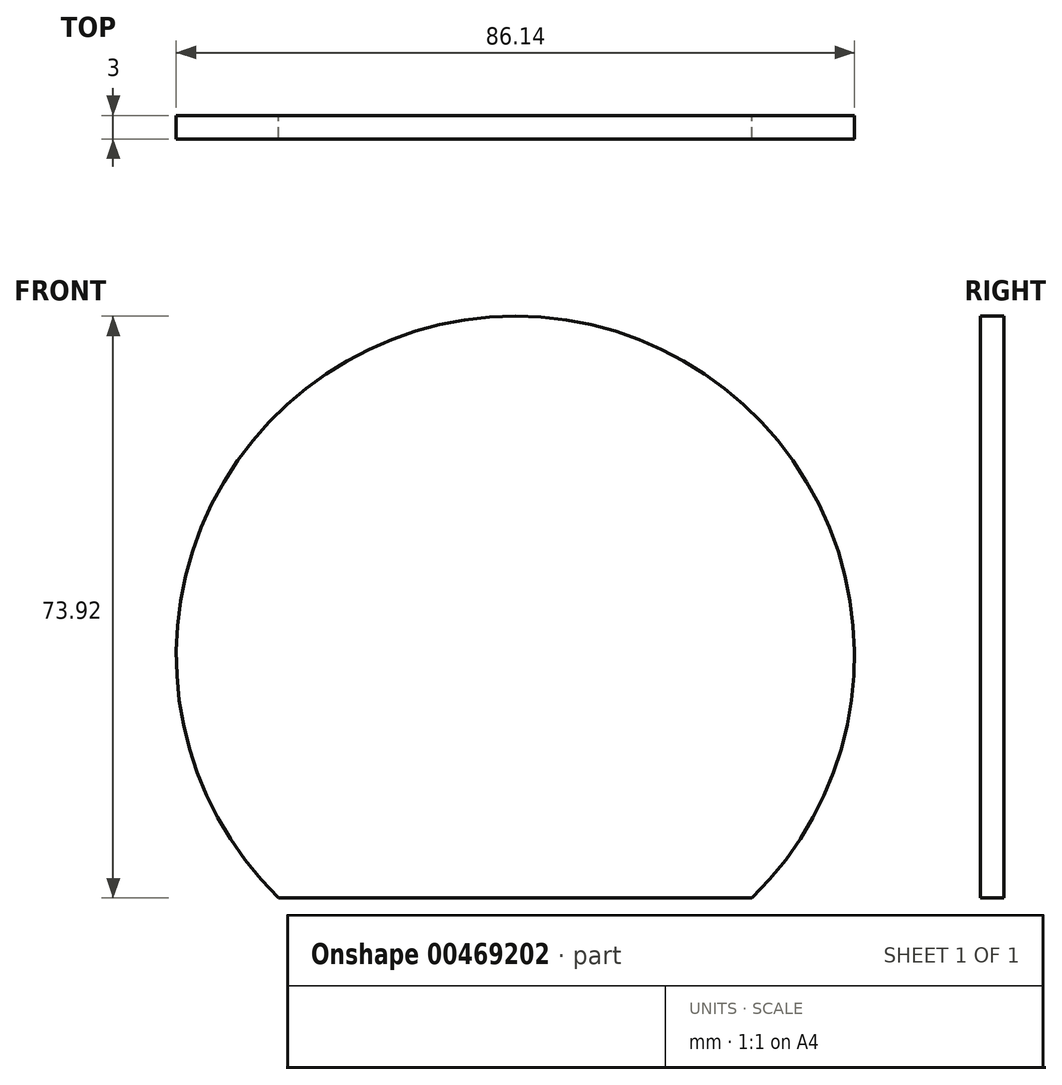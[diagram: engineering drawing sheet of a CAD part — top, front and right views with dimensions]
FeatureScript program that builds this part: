
annotation { "Feature Type Name" : "Feature", "Feature Type Description" : "" }
export const myFeature = defineFeature(function(context is Context, id is Id, definition is map)
    precondition{}
    {
        {
            var Q0;
            Q0=qCreatedBy(makeId("Front.planeOp"),FACE);
            var sketch = newSketch(context, id + "F0", { "sketchPlane" : qUnion([Q0])});
            skArc(sketch, "E0", {"start": v(30.05, -30.85) * mm, "mid": v(0, 43.07) * mm, "end": v(-30.05, -30.85) * mm});
            skLineSegment(sketch, "E1", {"start": v(-30.05, -30.85) * mm, "end": v(25.18, -30.85) * mm});
            skLineSegment(sketch, "E2", {"start": v(25.18, -30.85) * mm, "end": v(30.05, -30.85) * mm});
            skSolve(sketch);
        }
        {
            var Q0;
            Q0 = qSketchRegion(id + "F0", true);
            extrude(context, id + "F1", {"entities" : qUnion([Q0]), "depth" : 3 * mm});
        }
    });
